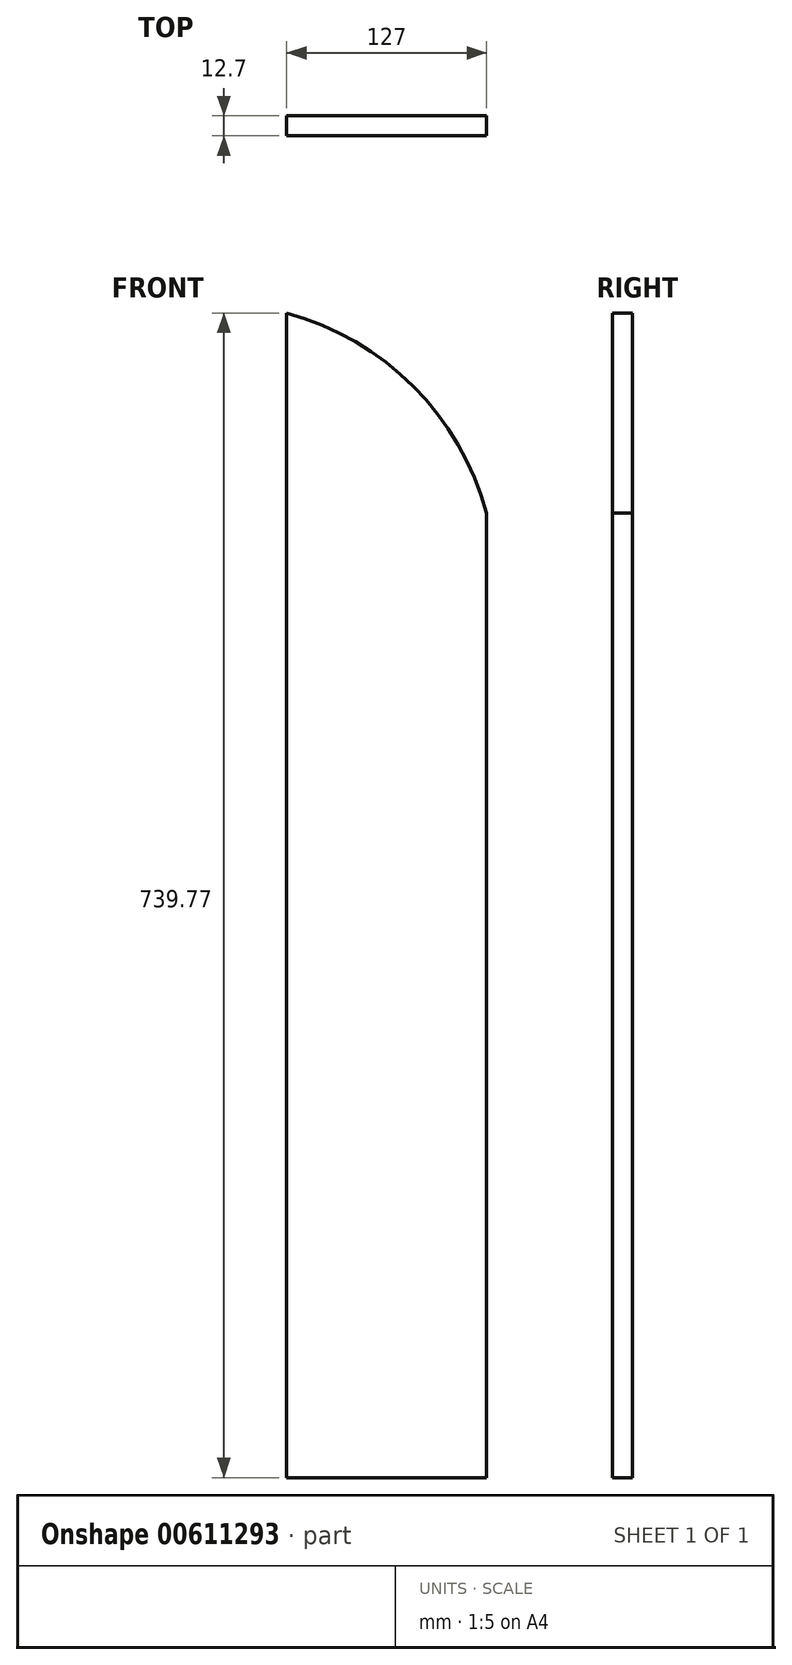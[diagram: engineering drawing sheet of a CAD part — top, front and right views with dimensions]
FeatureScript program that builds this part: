
annotation { "Feature Type Name" : "Feature", "Feature Type Description" : "" }
export const myFeature = defineFeature(function(context is Context, id is Id, definition is map)
    precondition{}
    {
        {
            var Q0;
            Q0=qCreatedBy(makeId("Front.planeOp"),FACE);
            var sketch = newSketch(context, id + "F0", { "sketchPlane" : qUnion([Q0])});
            skLineSegment(sketch, "E0.top", {"start": v(-127, -487.55) * mm, "end": v(0, -487.55) * mm});
            skLineSegment(sketch, "E0.left", {"start": v(-127, 252.22) * mm, "end": v(-127, -487.55) * mm});
            skLineSegment(sketch, "E0.right", {"start": v(0, 125.22) * mm, "end": v(0, -487.55) * mm});
            skArc(sketch, "E1.trimOffspring", {"start": v(0, 125.22) * mm, "mid": v(-46.66, 205.57) * mm, "end": v(-127, 252.22) * mm});
            skSolve(sketch);
        }
        {
            var Q0;
            Q0=makeQuery(id+"F0.imprint","IMPRINT",FACE,{"disambiguationData":[TD([[makeQuery(id+"F0.imprint","IMPRINT",EDGE,{"derivedFrom":sQuery(id+"F0.wireOp",EDGE,"E0.top")}),1.0]])]});
            extrude(context, id + "F1", {"entities" : qUnion([Q0]), "depth" : 12.7 * mm, "offsetDistance" : 25.4 * mm});
        }
    });
